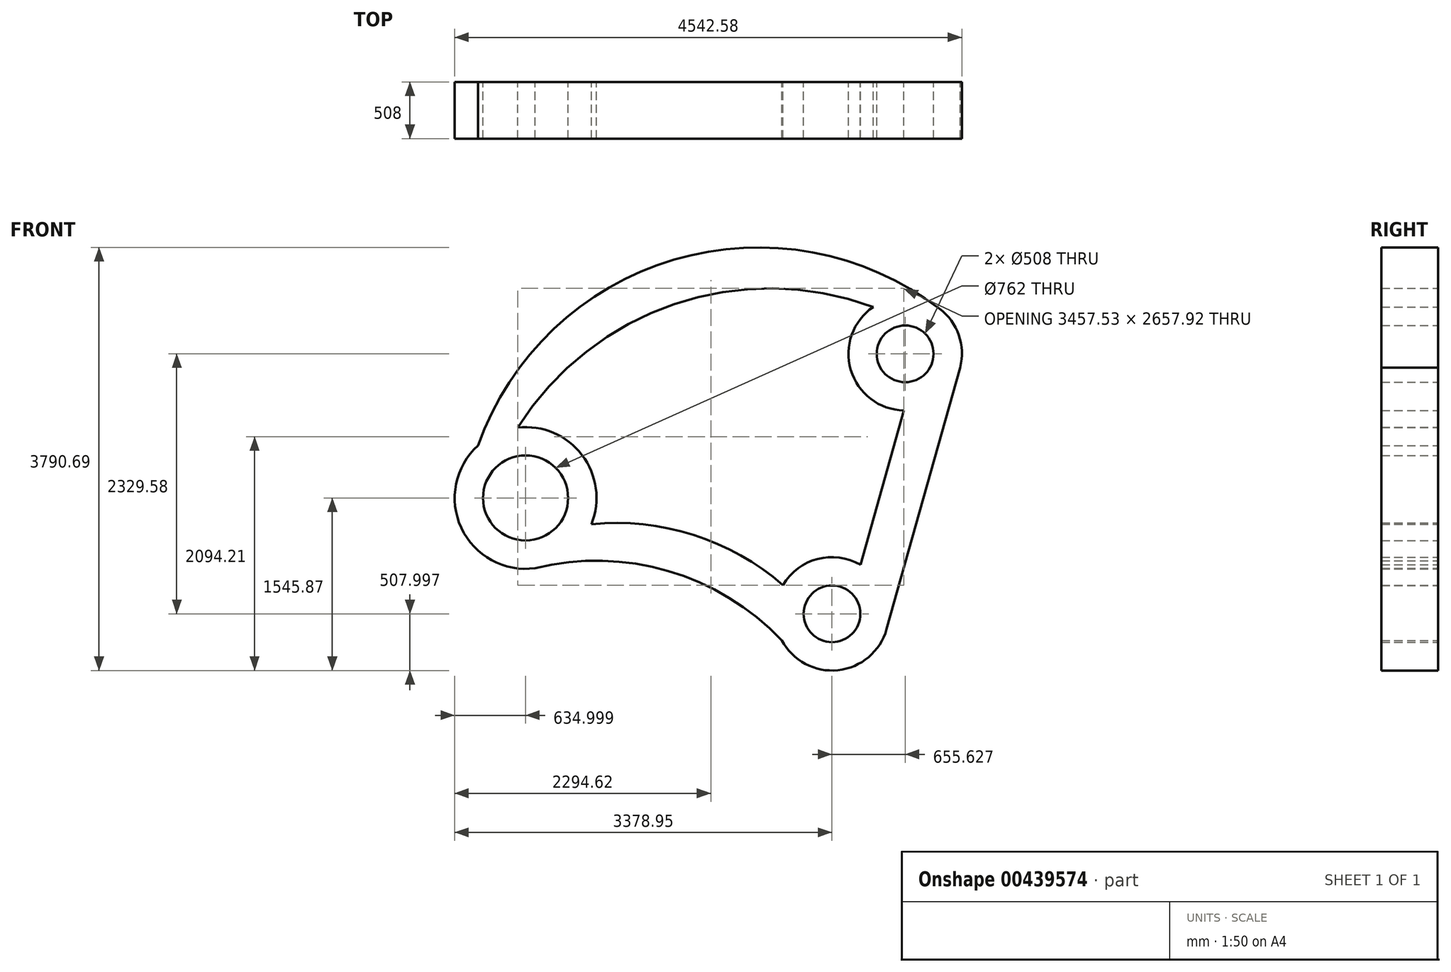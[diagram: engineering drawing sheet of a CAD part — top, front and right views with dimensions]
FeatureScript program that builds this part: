
annotation { "Feature Type Name" : "Feature", "Feature Type Description" : "" }
export const myFeature = defineFeature(function(context is Context, id is Id, definition is map)
    precondition{}
    {
        {
            var Q0;
            Q0=qCreatedBy(makeId("Front.planeOp"),FACE);
            var sketch = newSketch(context, id + "F0", { "sketchPlane" : qUnion([Q0])});
            skArc(sketch, "E0", {"start": v(-1178.44, 677.3) * mm, "mid": v(-1562.74, 729.59) * mm, "end": v(-1871.94, 495.45) * mm});
            skArc(sketch, "E1", {"start": v(-1064.05, 2987.77) * mm, "mid": v(-1265.39, 2423.62) * mm, "end": v(-789.46, 2059.9) * mm});
            skArc(sketch, "E2", {"start": v(-469.34, 2971.04) * mm, "mid": v(-2848.56, 3411.1) * mm, "end": v(-4604.46, 1746.42) * mm});
            skArc(sketch, "E3", {"start": v(-3587.58, 1041.96) * mm, "mid": v(-3672.78, 1660.94) * mm, "end": v(-4247, 1907.3) * mm});
            skArc(sketch, "E4", {"start": v(-1882.6, 0) * mm, "mid": v(-2900.28, 622.03) * mm, "end": v(-4092.76, 646.8) * mm});
            skLineSegment(sketch, "E5", {"start": v(-285.3, 2445.08) * mm, "end": v(-973.19, 0) * mm});
            skArc(sketch, "E6", {"start": v(-1064.05, 2987.77) * mm, "mid": v(-2847.16, 3012.08) * mm, "end": v(-4247, 1907.3) * mm});
            skLineSegment(sketch, "E7", {"start": v(-789.46, 2059.9) * mm, "end": v(-1178.44, 677.3) * mm});
            skArc(sketch, "E8", {"start": v(-1871.94, 495.45) * mm, "mid": v(-2673.69, 944.74) * mm, "end": v(-3587.58, 1041.96) * mm});
            skCircle(sketch, "E9", {"center": v(-4177.85, 1276.07) * mm, "radius": 381 * mm});
            skCircle(sketch, "E10", {"center": v(-778.27, 2567.77) * mm, "radius": 254 * mm});
            skCircle(sketch, "E11", {"center": v(-1433.9, 238.2) * mm, "radius": 254 * mm});
            skArc(sketch, "E12.trimOffspring", {"start": v(-293.65, 2415.44) * mm, "mid": v(-293.9, 2720.94) * mm, "end": v(-469.34, 2971.04) * mm});
            skArc(sketch, "E13.trimOffspring", {"start": v(-1882.6, 0) * mm, "mid": v(-1379.7, -266.9) * mm, "end": v(-944.88, 100.62) * mm});
            skArc(sketch, "E14.trimOffspring", {"start": v(-4604.46, 1746.42) * mm, "mid": v(-4728.7, 960.17) * mm, "end": v(-3987.35, 670.31) * mm});
            skLineSegment(sketch, "E15.trimOffspring", {"start": v(-3564.5, 1044.07) * mm, "end": v(-3583.92, 1051.42) * mm});
            skSolve(sketch);
        }
        {
            var Q0;
            {var subQ13=sQuery(id+"F0.wireOp",EDGE,"E0");Q0=makeQuery(id+"F0.imprint","IMPRINT",FACE,{"disambiguationData":[TD([[makeQuery(id+"F0.imprint","IMPRINT",EDGE,{"derivedFrom":subQ13}),1.0]])]});}
            extrude(context, id + "F1", {"entities" : qUnion([Q0]), "depth" : 508 * mm});
        }
    });
